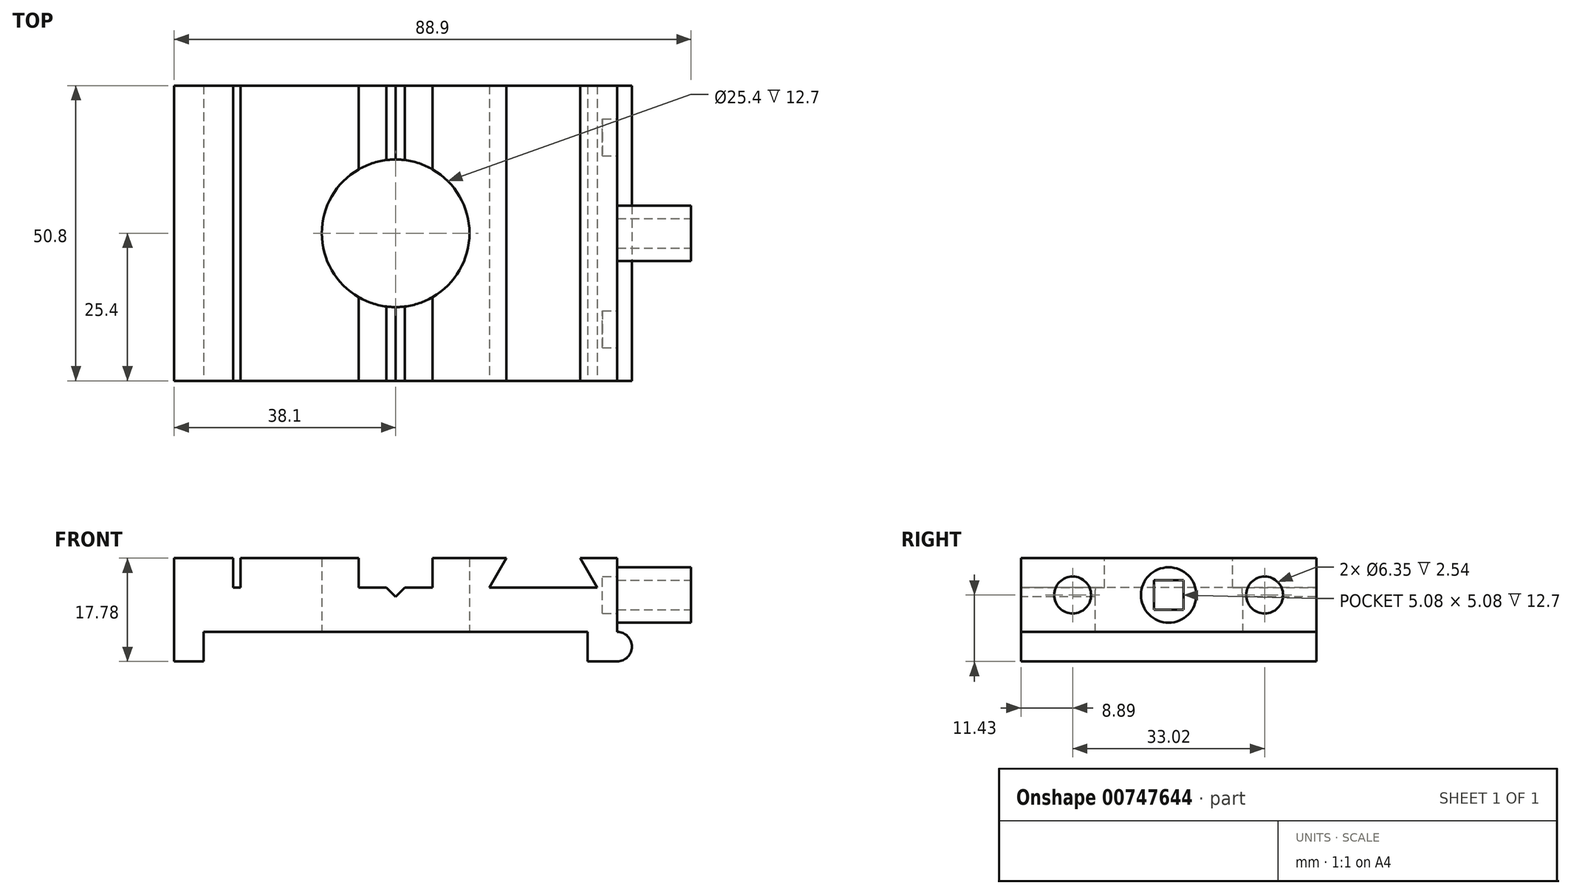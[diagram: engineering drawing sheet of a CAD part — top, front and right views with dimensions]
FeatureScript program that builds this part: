
annotation { "Feature Type Name" : "Feature", "Feature Type Description" : "" }
export const myFeature = defineFeature(function(context is Context, id is Id, definition is map)
    precondition{}
    {
        {
            var Q0;
            Q0=qCreatedBy(makeId("Top.planeOp"),FACE);
            var sketch = newSketch(context, id + "F0", { "sketchPlane" : qUnion([Q0])});
            skLineSegment(sketch, "E0.bottom", {"start": v(38.1, 25.4) * mm, "end": v(-38.1, 25.4) * mm});
            skLineSegment(sketch, "E0.top", {"start": v(38.1, -25.4) * mm, "end": v(-38.1, -25.4) * mm});
            skLineSegment(sketch, "E0.left", {"start": v(38.1, 25.4) * mm, "end": v(38.1, -25.4) * mm});
            skLineSegment(sketch, "E0.right", {"start": v(-38.1, 25.4) * mm, "end": v(-38.1, -25.4) * mm});
            skPoint(sketch, "E0.middle", {"position": v(0, 0) * mm});
            skCircle(sketch, "E1", {"center": v(0, 0) * mm, "radius": 12.7 * mm});
            skSolve(sketch);
        }
        {
            var Q0;
            Q0=makeQuery(id+"F0.imprint","IMPRINT",FACE,{"disambiguationData":[TD([[makeQuery(id+"F0.imprint","IMPRINT",EDGE,{"derivedFrom":sQuery(id+"F0.wireOp",EDGE,"E0.bottom")}),1.0]])]});
            extrude(context, id + "F1", {"entities" : qUnion([Q0]), "depth" : 12.7 * mm, "offsetDistance" : 25.4 * mm});
        }
        {
            var Q0;
            Q0=makeQuery(id+"F1.opExtrude","CAP_FACE",FACE,{"disambiguationData":[OSD([sQuery(id+"F0.wireOp",EDGE,"E0.bottom"),sQuery(id+"F0.wireOp",EDGE,"E0.top"),sQuery(id+"F0.wireOp",EDGE,"E0.left"),sQuery(id+"F0.wireOp",EDGE,"E0.right"),sQuery(id+"F0.wireOp",EDGE,"E1")])],"isStart":false});
            var sketch = newSketch(context, id + "F2", { "sketchPlane" : qUnion([Q0])});
            skLineSegment(sketch, "E2.bottom", {"start": v(-27.94, 25.4) * mm, "end": v(-26.67, 25.4) * mm});
            skLineSegment(sketch, "E2.top", {"start": v(-27.94, -25.4) * mm, "end": v(-26.67, -25.4) * mm});
            skLineSegment(sketch, "E2.left", {"start": v(-27.94, 25.4) * mm, "end": v(-27.94, -25.4) * mm});
            skLineSegment(sketch, "E2.right", {"start": v(-26.67, 25.4) * mm, "end": v(-26.67, -25.4) * mm});
            skLineSegment(sketch, "E3", {"start": v(-6.35, 25.4) * mm, "end": v(-6.35, -25.4) * mm});
            skLineSegment(sketch, "E4", {"start": v(-6.35, -25.4) * mm, "end": v(6.35, -25.4) * mm});
            skLineSegment(sketch, "E5", {"start": v(6.35, -25.4) * mm, "end": v(6.35, 25.4) * mm});
            skLineSegment(sketch, "E6", {"start": v(6.35, 25.4) * mm, "end": v(-6.35, 25.4) * mm});
            skPoint(sketch, "E7", {"position": v(0, 0) * mm});
            skLineSegment(sketch, "E8", {"start": v(0, 25.4) * mm, "end": v(0, -25.4) * mm, "construction": true});
            skSolve(sketch);
        }
        {
            var Q0;
            Q0=makeQuery(id+"F2.imprint","IMPRINT",FACE,{"disambiguationData":[TD([[makeQuery(id+"F2.imprint","IMPRINT",EDGE,{"derivedFrom":sQuery(id+"F2.wireOp",EDGE,"E2.bottom")}),1.0]])]});
            var Q1;
            {var subQ0=sQuery(id+"F2.wireOp",EDGE,"E4");Q1=makeQuery(id+"F2.imprint","IMPRINT",FACE,{"disambiguationData":[TD([[makeQuery(id+"F2.imprint","IMPRINT",EDGE,{"derivedFrom":subQ0}),-1.0]])]});}
            var Q2;
            {var subQ0=sQuery(id+"F2.wireOp",EDGE,"E6");Q2=makeQuery(id+"F2.imprint","IMPRINT",FACE,{"disambiguationData":[TD([[makeQuery(id+"F2.imprint","IMPRINT",EDGE,{"derivedFrom":subQ0}),1.0]])]});}
            extrude(context, id + "F3", {"entities" : qUnion([Q0, Q1, Q2]), "operationType" : NewBodyOperationType.REMOVE, "oppositeDirection" : true, "depth" : 5.08 * mm});
        }
        {
            var Q0;
            Q0=makeQuery(id+"F1.opExtrude","SWEPT_FACE",FACE,{"disambiguationData":[OSD([sQuery(id+"F0.wireOp",EDGE,"E0.top")])]});
            var sketch = newSketch(context, id + "F4", { "sketchPlane" : qUnion([Q0])});
            skLineSegment(sketch, "E9", {"start": v(19.05, 12.7) * mm, "end": v(16.12, 7.62) * mm});
            skLineSegment(sketch, "E10", {"start": v(16.12, 7.62) * mm, "end": v(34.68, 7.62) * mm});
            skLineSegment(sketch, "E11", {"start": v(34.68, 7.62) * mm, "end": v(31.75, 12.7) * mm});
            skLineSegment(sketch, "E12", {"start": v(31.75, 12.7) * mm, "end": v(19.05, 12.7) * mm});
            skLineSegment(sketch, "E13", {"start": v(25.4, 7.62) * mm, "end": v(25.4, 12.7) * mm, "construction": true});
            skSolve(sketch);
        }
        {
            var Q0;
            Q0=makeQuery(id+"F4.imprint","IMPRINT",FACE,{"disambiguationData":[TD([[makeQuery(id+"F4.imprint","IMPRINT",EDGE,{"derivedFrom":sQuery(id+"F4.wireOp",EDGE,"E9")}),1.0]])]});
            extrude(context, id + "F5", {"entities" : qUnion([Q0]), "operationType" : NewBodyOperationType.REMOVE, "endBound" : BoundingType.THROUGH_ALL, "oppositeDirection" : true, "depth" : 25.4 * mm});
        }
        {
            var Q0;
            Q0=makeQuery(id+"F1.opExtrude","SWEPT_FACE",FACE,{"disambiguationData":[OSD([sQuery(id+"F0.wireOp",EDGE,"E0.left")])]});
            var sketch = newSketch(context, id + "F6", { "sketchPlane" : qUnion([Q0])});
            skCircle(sketch, "E14", {"center": v(0, 6.35) * mm, "radius": 4.76 * mm});
            skPoint(sketch, "E14.centerSnap0", {"position": v(-25.4, 6.35) * mm});
            skPoint(sketch, "E14.centerSnap1", {"position": v(0, 12.7) * mm});
            skSolve(sketch);
        }
        {
            var Q0;
            Q0=makeQuery(id+"F6.imprint","IMPRINT",FACE,{"disambiguationData":[TD([[makeQuery(id+"F6.imprint","IMPRINT",EDGE,{"derivedFrom":sQuery(id+"F6.wireOp",EDGE,"E14")}),1.0]])]});
            extrude(context, id + "F7", {"entities" : qUnion([Q0]), "operationType" : NewBodyOperationType.ADD, "depth" : 12.7 * mm});
        }
        {
            var Q0;
            Q0=makeQuery(id+"F1.opExtrude","CAP_FACE",FACE,{"disambiguationData":[OSD([sQuery(id+"F0.wireOp",EDGE,"E0.bottom"),sQuery(id+"F0.wireOp",EDGE,"E0.top"),sQuery(id+"F0.wireOp",EDGE,"E0.left"),sQuery(id+"F0.wireOp",EDGE,"E0.right"),sQuery(id+"F0.wireOp",EDGE,"E1")])],"isStart":true});
            var sketch = newSketch(context, id + "F8", { "sketchPlane" : qUnion([Q0])});
            skLineSegment(sketch, "E15.bottom", {"start": v(-38.1, -25.4) * mm, "end": v(-33.02, -25.4) * mm});
            skLineSegment(sketch, "E15.top", {"start": v(-38.1, 25.4) * mm, "end": v(-33.02, 25.4) * mm});
            skLineSegment(sketch, "E15.left", {"start": v(-38.1, -25.4) * mm, "end": v(-38.1, 25.4) * mm});
            skLineSegment(sketch, "E15.right", {"start": v(-33.02, -25.4) * mm, "end": v(-33.02, 25.4) * mm});
            skLineSegment(sketch, "E16.bottom", {"start": v(38.1, -25.4) * mm, "end": v(33.02, -25.4) * mm});
            skLineSegment(sketch, "E16.top", {"start": v(38.1, 25.4) * mm, "end": v(33.02, 25.4) * mm});
            skLineSegment(sketch, "E16.left", {"start": v(38.1, -25.4) * mm, "end": v(38.1, 25.4) * mm});
            skLineSegment(sketch, "E16.right", {"start": v(33.02, -25.4) * mm, "end": v(33.02, 25.4) * mm});
            skSolve(sketch);
        }
        {
            var Q0;
            Q0=makeQuery(id+"F8.imprint","IMPRINT",FACE,{"disambiguationData":[TD([[makeQuery(id+"F8.imprint","IMPRINT",EDGE,{"derivedFrom":sQuery(id+"F8.wireOp",EDGE,"E15.bottom")}),-1.0]])]});
            var Q1;
            Q1=makeQuery(id+"F8.imprint","IMPRINT",FACE,{"disambiguationData":[TD([[makeQuery(id+"F8.imprint","IMPRINT",EDGE,{"derivedFrom":sQuery(id+"F8.wireOp",EDGE,"E16.bottom")}),-1.0]])]});
            extrude(context, id + "F9", {"entities" : qUnion([Q0, Q1]), "operationType" : NewBodyOperationType.ADD, "depth" : 5.08 * mm, "offsetDistance" : 25.4 * mm});
        }
        {
            var Q0;
            Q0=makeQuery(id+"F7.opExtrude","CAP_FACE",FACE,{"disambiguationData":[OSD([sQuery(id+"F6.wireOp",EDGE,"E14")])],"isStart":false});
            var sketch = newSketch(context, id + "F10", { "sketchPlane" : qUnion([Q0])});
            skLineSegment(sketch, "E17.bottom", {"start": v(2.54, 8.9) * mm, "end": v(-2.54, 8.9) * mm});
            skLineSegment(sketch, "E17.top", {"start": v(2.54, 3.81) * mm, "end": v(-2.54, 3.81) * mm});
            skLineSegment(sketch, "E17.left", {"start": v(2.54, 8.9) * mm, "end": v(2.54, 3.81) * mm});
            skLineSegment(sketch, "E17.right", {"start": v(-2.54, 8.9) * mm, "end": v(-2.54, 3.81) * mm});
            skPoint(sketch, "E17.middle", {"position": v(0, 6.35) * mm});
            skSolve(sketch);
        }
        {
            var Q0;
            Q0 = qSketchRegion(id + "F10", true);
            extrude(context, id + "F11", {"entities" : qUnion([Q0]), "operationType" : NewBodyOperationType.REMOVE, "oppositeDirection" : true, "depth" : 12.7 * mm, "offsetDistance" : 25.4 * mm});
        }
        {
            var Q0;
            Q0=makeQuery(id+"F9.boolean.opBoolean","MERGE",FACE,{"derivedFrom":[makeQuery(id+"F1.opExtrude","SWEPT_FACE",FACE,{"disambiguationData":[OSD([sQuery(id+"F0.wireOp",EDGE,"E0.top")])]}),makeQuery(id+"F9.opExtrude","SWEPT_FACE",FACE,{"disambiguationData":[OSD([sQuery(id+"F8.wireOp",EDGE,"E15.top")])]}),makeQuery(id+"F9.opExtrude","SWEPT_FACE",FACE,{"disambiguationData":[OSD([sQuery(id+"F8.wireOp",EDGE,"E16.top")])]})]});
            var sketch = newSketch(context, id + "F12", { "sketchPlane" : qUnion([Q0])});
            skLineSegment(sketch, "E18", {"start": v(38.1, -5.08) * mm, "end": v(38.1, -2.54) * mm, "construction": true});
            skCircle(sketch, "E19", {"center": v(38.1, -2.54) * mm, "radius": 2.54 * mm});
            skSolve(sketch);
        }
        {
            var Q0;
            {var subQ0=sQuery(id+"F12.wireOp",EDGE,"E19");var subQ1=sQuery(id+"F8.wireOp",EDGE,"E16.top");var subQ2=makeQuery(id+"F9.boolean.opBoolean","MERGE",EDGE,{"derivedFrom":[makeQuery(id+"F1.opExtrude","SWEPT_EDGE",EDGE,{"disambiguationData":[OSD([sQuery(id+"F0.wireOp",EDGE,"E0.top"),sQuery(id+"F0.wireOp",EDGE,"E0.left")])]}),makeQuery(id+"F9.opExtrude","SWEPT_EDGE",EDGE,{"disambiguationData":[OSD([subQ1,sQuery(id+"F8.wireOp",EDGE,"E16.left")])]})]});var subQ4=makeQuery(id+"F12.imprint","INTERSECT",VERTEX,{"derivedFrom":[subQ2,subQ0]});Q0=makeQuery(id+"F12.imprint","IMPRINT",FACE,{"disambiguationData":[TD([[makeQuery(id+"F12.imprint","IMPRINT",EDGE,{"disambiguationData":[TD([[subQ4,1.0]])],"derivedFrom":subQ0}),1.0]])]});}
            var Q1;
            Q1=sQuery(id+"F12.wireOp",EDGE,"E19");
            var Q2;
            Q2=makeQuery(id+"F9.boolean.opBoolean","MERGE",FACE,{"derivedFrom":[makeQuery(id+"F1.opExtrude","SWEPT_FACE",FACE,{"disambiguationData":[OSD([sQuery(id+"F0.wireOp",EDGE,"E0.bottom")])]}),makeQuery(id+"F9.opExtrude","SWEPT_FACE",FACE,{"disambiguationData":[OSD([sQuery(id+"F8.wireOp",EDGE,"E15.bottom")])]}),makeQuery(id+"F9.opExtrude","SWEPT_FACE",FACE,{"disambiguationData":[OSD([sQuery(id+"F8.wireOp",EDGE,"E16.bottom")])]})]});
            extrude(context, id + "F13", {"entities" : qUnion([Q0]), "operationType" : NewBodyOperationType.ADD, "surfaceOperationType" : NewSurfaceOperationType.ADD, "surfaceEntities" : qUnion([Q1]), "endBound" : BoundingType.UP_TO_SURFACE, "oppositeDirection" : true, "depth" : 25.4 * mm, "endBoundEntityFace" : qUnion([Q2]), "offsetDistance" : 25.4 * mm});
        }
        {
            var Q0;
            Q0=makeQuery(id+"F9.boolean.opBoolean","MERGE",FACE,{"derivedFrom":[makeQuery(id+"F1.opExtrude","SWEPT_FACE",FACE,{"disambiguationData":[OSD([sQuery(id+"F0.wireOp",EDGE,"E0.left")])]}),makeQuery(id+"F9.opExtrude","SWEPT_FACE",FACE,{"disambiguationData":[OSD([sQuery(id+"F8.wireOp",EDGE,"E16.left")])]})]});
            var sketch = newSketch(context, id + "F14", { "sketchPlane" : qUnion([Q0])});
            skCircle(sketch, "E20.MirrorC", {"center": v(-16.51, 6.35) * mm, "radius": 3.18 * mm});
            skCircle(sketch, "E21.MirrorC", {"center": v(16.51, 6.35) * mm, "radius": 3.18 * mm});
            skLineSegment(sketch, "E22", {"start": v(0, 12.7) * mm, "end": v(0, 0) * mm});
            skSolve(sketch);
        }
        {
            var Q0;
            Q0 = qSketchRegion(id + "F14", true);
            extrude(context, id + "F15", {"entities" : qUnion([Q0]), "operationType" : NewBodyOperationType.REMOVE, "oppositeDirection" : true, "depth" : 2.54 * mm, "offsetDistance" : 25.4 * mm});
        }
        {
            var Q0;
            {var subQ0=sQuery(id+"F12.wireOp",EDGE,"E19");var subQ1=sQuery(id+"F8.wireOp",EDGE,"E16.left");var subQ2=sQuery(id+"F8.wireOp",EDGE,"E16.top");var subQ3=sQuery(id+"F0.wireOp",EDGE,"E0.left");var subQ4=sQuery(id+"F0.wireOp",EDGE,"E0.top");Q0=makeQuery(id+"F5AVaeNxJRF913x_1.1.F13.boolean.opBoolean","MERGE",FACE,{"derivedFrom":[makeQuery(id+"F13.boolean.opBoolean","MERGE",FACE,{"derivedFrom":[makeQuery(id+"F9.boolean.opBoolean","MERGE",FACE,{"derivedFrom":[makeQuery(id+"F1.opExtrude","SWEPT_FACE",FACE,{"disambiguationData":[OSD([subQ4])]}),makeQuery(id+"F9.opExtrude","SWEPT_FACE",FACE,{"disambiguationData":[OSD([sQuery(id+"F8.wireOp",EDGE,"E15.top")])]}),makeQuery(id+"F9.opExtrude","SWEPT_FACE",FACE,{"disambiguationData":[OSD([subQ2])]})]}),makeQuery(id+"F13.opExtrude","CAP_FACE",FACE,{"disambiguationData":[OSD([subQ4,subQ3,subQ2,subQ1,subQ0])],"isStart":true})]}),makeQuery(id+"F5AVaeNxJRF913x_1.1.F13.opExtrude","CAP_FACE",FACE,{"disambiguationData":[OSD([subQ4,subQ3,subQ2,subQ1,subQ0])],"isStart":true})]});}
            var sketch = newSketch(context, id + "F16", { "sketchPlane" : qUnion([Q0])});
            skLineSegment(sketch, "E23", {"start": v(0, 6.03) * mm, "end": v(-1.59, 7.62) * mm});
            skLineSegment(sketch, "E24", {"start": v(0, 6.03) * mm, "end": v(1.59, 7.62) * mm});
            skSolve(sketch);
        }
        {
            var Q0;
            {var subQ0=sQuery(id+"F16.wireOp",EDGE,"E23");Q0=makeQuery(id+"F16.imprint","IMPRINT",FACE,{"disambiguationData":[TD([[makeQuery(id+"F16.imprint","IMPRINT",EDGE,{"derivedFrom":subQ0}),-1.0]])]});}
            var Q1;
            {var subQ0=sQuery(id+"F8.wireOp",EDGE,"E16.bottom");var subQ1=sQuery(id+"F8.wireOp",EDGE,"E15.bottom");var subQ2=sQuery(id+"F0.wireOp",EDGE,"E0.bottom");Q1=makeQuery(id+"F5AVaeNxJRF913x_1.1.F13.boolean.opBoolean","MERGE",FACE,{"derivedFrom":[makeQuery(id+"F13.boolean.opBoolean","MERGE",FACE,{"derivedFrom":[makeQuery(id+"F9.boolean.opBoolean","MERGE",FACE,{"derivedFrom":[makeQuery(id+"F1.opExtrude","SWEPT_FACE",FACE,{"disambiguationData":[OSD([subQ2])]}),makeQuery(id+"F9.opExtrude","SWEPT_FACE",FACE,{"disambiguationData":[OSD([subQ1])]}),makeQuery(id+"F9.opExtrude","SWEPT_FACE",FACE,{"disambiguationData":[OSD([subQ0])]})]}),makeQuery(id+"F13.opExtrude","CAP_FACE",FACE,{"disambiguationData":[OSD([subQ2,subQ1,subQ0])],"isStart":false})]}),makeQuery(id+"F5AVaeNxJRF913x_1.1.F13.opExtrude","CAP_FACE",FACE,{"disambiguationData":[OSD([subQ2,subQ1,subQ0])],"isStart":false})]});}
            extrude(context, id + "F17", {"entities" : qUnion([Q0]), "operationType" : NewBodyOperationType.REMOVE, "endBound" : BoundingType.UP_TO_SURFACE, "oppositeDirection" : true, "depth" : 25.4 * mm, "endBoundEntityFace" : qUnion([Q1]), "offsetDistance" : 25.4 * mm});
        }
    });
